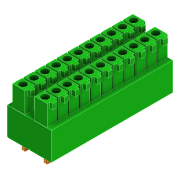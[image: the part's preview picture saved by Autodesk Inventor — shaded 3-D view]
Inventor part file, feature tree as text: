
AUTODESK INVENTOR PART (.ipt)
format: ipt  version: 2022 (Build 260153000, 153)  size: 577,536 bytes
history: native  units: mm
features: sketch x12, extrude x8, pattern_linear x2, fillet x1
ambient origin geometry x8: Origin, YZ Plane, XZ Plane, XY Plane, X Axis, Y Axis, Z Axis, Center Point
bodies: Solid1 (feature_tree), Solid2 (feature_tree)
feature tree (23):
  extrude  "Extrusion1"  Depth=2.0mm
  extrude  "Extrusion2"  Depth=7.5mm TaperAngle=0.0deg
  extrude  "Extrusion3"  Depth=0.25mm
  extrude  "Extrusion4"  Depth=2.0mm
  extrude  "Extrusion5"  Depth=4.0mm
  extrude  "Extrusion6"  Depth=2.7mm
  extrude  "Extrusion7"  Depth=8.0mm TaperAngle=0.0deg
  extrude  "Extrusion8"  Depth=0.4mm
  fillet  "Fillet1"  Radius=0.4mm
  pattern_linear  "Rectangular Pattern1"  Count1=11 Spacing1=4.0mm
  pattern_linear  "Rectangular Pattern2"  Count1=2 Spacing1=8.0mm
  sketch  "Sketch9"  dims[d24=1.0mm d25=0.0mm]
  sketch  "Sketch10"  dims[d26=0.5mm d27=110.0mm d29=4.0mm d30=20.0mm d32=8.0mm]
  sketch  "Sketch11"  dims[d33=110.0mm d35=4.0mm]
  sketch  "Sketch12"  dims[d36=20.0mm d38=8.0mm]
  sketch  "Sketch1"  dims[d0=7.5mm d1=0.0mm d2=2.0mm]
  sketch  "Sketch2"  dims[d3=7.5mm d4=0.0mm d5=7.5mm d6=0.0mm]
  sketch  "Sketch3"  dims[d7=7.5mm d8=0.0mm d9=0.25mm]
  sketch  "Sketch4"  dims[d10=10.0mm d11=0.0mm d12=2.0mm]
  sketch  "Sketch5"  dims[d13=2.0mm d14=4.0mm]
  sketch  "Sketch6"  dims[d15=2.7mm d16=2.7mm]
  sketch  "Sketch7"  dims[d17=2.7mm d18=8.0mm d19=0.0mm]
  sketch  "Sketch8"  dims[d20=9.0mm d21=0.0mm d22=0.4mm d23=0.4mm]
